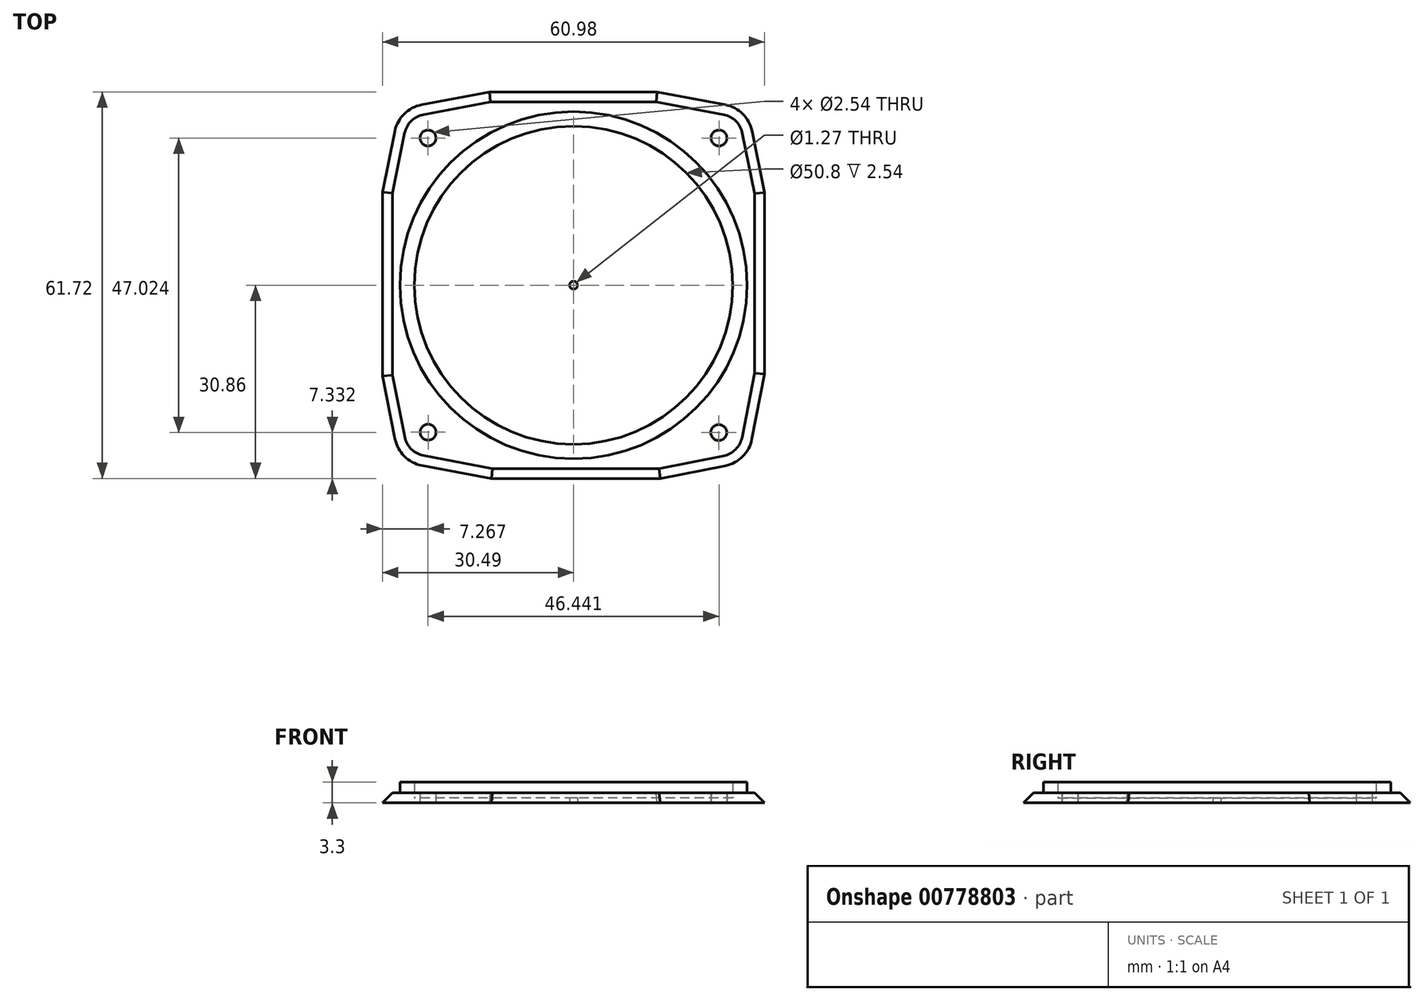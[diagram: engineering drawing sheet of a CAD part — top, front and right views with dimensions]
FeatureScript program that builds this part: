
annotation { "Feature Type Name" : "Feature", "Feature Type Description" : "" }
export const myFeature = defineFeature(function(context is Context, id is Id, definition is map)
    precondition{}
    {
        {
            var Q0;
            Q0=qCreatedBy(makeId("Top.planeOp"),FACE);
            var sketch = newSketch(context, id + "F0", { "sketchPlane" : qUnion([Q0])});
            skCircle(sketch, "E0", {"center": v(0, 0) * mm, "radius": 25.4 * mm});
            skCircle(sketch, "E1", {"center": v(0, 0) * mm, "radius": 27.7 * mm});
            skLineSegment(sketch, "E2.bottom", {"start": v(-13.5, 31.82) * mm, "end": v(13.46, 31.82) * mm});
            skLineSegment(sketch, "E2.top", {"start": v(-13.16, -31.82) * mm, "end": v(13.92, -31.82) * mm});
            skLineSegment(sketch, "E2.left", {"start": v(-31.44, 14.95) * mm, "end": v(-31.44, -14.63) * mm});
            skLineSegment(sketch, "E2.right", {"start": v(31.44, 14.88) * mm, "end": v(31.44, -14.3) * mm});
            skPoint(sketch, "E3.visualSharp", {"position": v(-31.44, 31.82) * mm});
            skPoint(sketch, "E4.visualSharp", {"position": v(31.44, 31.82) * mm});
            skPoint(sketch, "E5.visualSharp", {"position": v(31.44, -31.82) * mm});
            skPoint(sketch, "E6.visualSharp", {"position": v(-31.44, -31.82) * mm});
            skPoint(sketch, "E7", {"position": v(28.6, 28.94) * mm});
            skPoint(sketch, "E8", {"position": v(28.6, -28.94) * mm});
            skPoint(sketch, "E9", {"position": v(-28.6, -28.94) * mm});
            skLineSegment(sketch, "E10", {"start": v(-26.8, 27.11) * mm, "end": v(26.8, -27.11) * mm});
            skLineSegment(sketch, "E11", {"start": v(-26.8, -27.11) * mm, "end": v(26.8, 27.11) * mm});
            skPoint(sketch, "E12", {"position": v(-26.8, 27.11) * mm});
            skPoint(sketch, "E13", {"position": v(26.8, 27.11) * mm});
            skPoint(sketch, "E14", {"position": v(26.8, -27.11) * mm});
            skPoint(sketch, "E15", {"position": v(-26.8, -27.11) * mm});
            skPoint(sketch, "E16.orphan", {"position": v(-28.6, 28.94) * mm});
            skLineSegment(sketch, "E17", {"start": v(-31.44, 14.95) * mm, "end": v(-29.44, 24.76) * mm});
            skLineSegment(sketch, "E18", {"start": v(-13.5, 31.82) * mm, "end": v(-24.41, 29.73) * mm});
            skLineSegment(sketch, "E19", {"start": v(13.46, 31.82) * mm, "end": v(24.4, 29.73) * mm});
            skLineSegment(sketch, "E20", {"start": v(31.44, 14.88) * mm, "end": v(29.44, 24.76) * mm});
            skLineSegment(sketch, "E21", {"start": v(-29.43, -24.72) * mm, "end": v(-31.44, -14.63) * mm});
            skLineSegment(sketch, "E22", {"start": v(-24.37, -29.72) * mm, "end": v(-13.16, -31.82) * mm});
            skLineSegment(sketch, "E23", {"start": v(31.44, -14.3) * mm, "end": v(29.41, -24.74) * mm});
            skLineSegment(sketch, "E24", {"start": v(13.92, -31.82) * mm, "end": v(24.4, -29.76) * mm});
            skLineSegment(sketch, "E25", {"start": v(-26.8, 27.11) * mm, "end": v(-28.6, 28.94) * mm});
            skLineSegment(sketch, "E26", {"start": v(26.8, 27.11) * mm, "end": v(28.6, 28.94) * mm});
            skLineSegment(sketch, "E27", {"start": v(28.6, -28.94) * mm, "end": v(26.8, -27.11) * mm});
            skLineSegment(sketch, "E28", {"start": v(-26.8, -27.11) * mm, "end": v(-28.6, -28.94) * mm});
            skArc(sketch, "E29.filletArc", {"start": v(-24.41, 29.73) * mm, "mid": v(-27.68, 28.01) * mm, "end": v(-29.44, 24.76) * mm});
            skArc(sketch, "E30.filletArc", {"start": v(29.44, 24.76) * mm, "mid": v(27.68, 28.01) * mm, "end": v(24.4, 29.73) * mm});
            skArc(sketch, "E31.filletArc", {"start": v(-29.43, -24.72) * mm, "mid": v(-27.67, -28) * mm, "end": v(-24.37, -29.72) * mm});
            skArc(sketch, "E32.filletArc", {"start": v(24.4, -29.76) * mm, "mid": v(27.67, -28.01) * mm, "end": v(29.41, -24.74) * mm});
            skPoint(sketch, "E33", {"position": v(25, -25.3) * mm});
            skPoint(sketch, "E34", {"position": v(-25, -25.3) * mm});
            skCircle(sketch, "E35", {"center": v(-23.22, 23.5) * mm, "radius": 1.27 * mm});
            skCircle(sketch, "E36", {"center": v(23.22, 23.5) * mm, "radius": 1.27 * mm});
            skCircle(sketch, "E37", {"center": v(-23.2, -23.48) * mm, "radius": 1.27 * mm});
            skCircle(sketch, "E38", {"center": v(23.18, -23.53) * mm, "radius": 1.27 * mm});
            skCircle(sketch, "E39", {"center": v(0, 0) * mm, "radius": 0.64 * mm});
            skSolve(sketch);
        }
        {
            var Q0;
            Q0=makeQuery(id+"F0.imprint","IMPRINT",FACE,{"disambiguationData":[TD([[makeQuery(id+"F0.imprint","IMPRINT",EDGE,{"derivedFrom":sQuery(id+"F0.wireOp",EDGE,"E0")}),1.0]])]});
            extrude(context, id + "F1", {"entities" : qUnion([Q0]), "depth" : 0.76 * mm, "offsetDistance" : 25.4 * mm});
        }
        {
            var Q0;
            Q0=makeQuery(id+"F0.imprint","IMPRINT",FACE,{"disambiguationData":[TD([[makeQuery(id+"F0.imprint","IMPRINT",EDGE,{"derivedFrom":sQuery(id+"F0.wireOp",EDGE,"E0")}),-1.0]])]});
            extrude(context, id + "F2", {"entities" : qUnion([Q0]), "operationType" : NewBodyOperationType.ADD, "depth" : 3.3 * mm, "offsetDistance" : 25.4 * mm});
        }
        {
            var Q0;
            Q0=makeQuery(id+"F0.imprint","IMPRINT",FACE,{"disambiguationData":[TD([[makeQuery(id+"F0.imprint","IMPRINT",EDGE,{"derivedFrom":sQuery(id+"F0.wireOp",EDGE,"E1")}),-1.0]])]});
            extrude(context, id + "F3", {"entities" : qUnion([Q0]), "operationType" : NewBodyOperationType.ADD, "depth" : 1.59 * mm, "offsetDistance" : 25.4 * mm});
        }
        {
            var Q0;
            Q0=makeQuery(id+"F3.opExtrude","CAP_EDGE",EDGE,{"disambiguationData":[OSD([sQuery(id+"F0.wireOp",EDGE,"E2.left")])],"isStart":false});
            var Q1;
            Q1=makeQuery(id+"F3.opExtrude","CAP_EDGE",EDGE,{"disambiguationData":[OSD([sQuery(id+"F0.wireOp",EDGE,"E21")])],"isStart":false});
            var Q2;
            Q2=makeQuery(id+"F3.opExtrude","CAP_EDGE",EDGE,{"disambiguationData":[OSD([sQuery(id+"F0.wireOp",EDGE,"E22")])],"isStart":false});
            var Q3;
            Q3=makeQuery(id+"F3.opExtrude","CAP_EDGE",EDGE,{"disambiguationData":[OSD([sQuery(id+"F0.wireOp",EDGE,"E2.top")])],"isStart":false});
            var Q4;
            Q4=makeQuery(id+"F3.opExtrude","CAP_EDGE",EDGE,{"disambiguationData":[OSD([sQuery(id+"F0.wireOp",EDGE,"E17")])],"isStart":false});
            var Q5;
            Q5=makeQuery(id+"F3.opExtrude","CAP_EDGE",EDGE,{"disambiguationData":[OSD([sQuery(id+"F0.wireOp",EDGE,"E18")])],"isStart":false});
            var Q6;
            Q6=makeQuery(id+"F3.opExtrude","CAP_EDGE",EDGE,{"disambiguationData":[OSD([sQuery(id+"F0.wireOp",EDGE,"E2.bottom")])],"isStart":false});
            var Q7;
            Q7=makeQuery(id+"F3.opExtrude","CAP_EDGE",EDGE,{"disambiguationData":[OSD([sQuery(id+"F0.wireOp",EDGE,"E19")])],"isStart":false});
            var Q8;
            Q8=makeQuery(id+"F3.opExtrude","CAP_EDGE",EDGE,{"disambiguationData":[OSD([sQuery(id+"F0.wireOp",EDGE,"E20")])],"isStart":false});
            var Q9;
            Q9=makeQuery(id+"F3.opExtrude","CAP_EDGE",EDGE,{"disambiguationData":[OSD([sQuery(id+"F0.wireOp",EDGE,"E2.right")])],"isStart":false});
            var Q10;
            Q10=makeQuery(id+"F3.opExtrude","CAP_EDGE",EDGE,{"disambiguationData":[OSD([sQuery(id+"F0.wireOp",EDGE,"E23")])],"isStart":false});
            var Q11;
            Q11=makeQuery(id+"F3.opExtrude","CAP_EDGE",EDGE,{"disambiguationData":[OSD([sQuery(id+"F0.wireOp",EDGE,"E24")])],"isStart":false});
            chamfer(context, id + "F4", {"entities" : qUnion([Q0, Q1, Q2, Q3, Q4, Q5, Q6, Q7, Q8, Q9, Q10, Q11]), "width" : 2.54 * mm, "tangentPropagation" : true});
        }
    });
